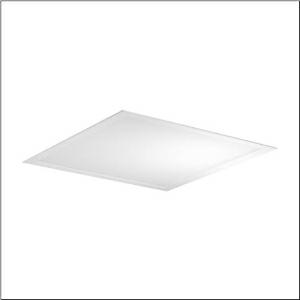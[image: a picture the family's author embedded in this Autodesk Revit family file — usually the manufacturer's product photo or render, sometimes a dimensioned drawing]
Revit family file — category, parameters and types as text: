
# Revit family: apollon_21_square_51mq11wd2114
name_source: partatom
category: Lighting Fixtures
units: mm (PartAtom-declared; Revit-internal decimal feet)

## family parameters
Cut with Voids When Loaded = No
Host = Face
Light Source = No
Part Type = Normal
Room Calculation Point = No
Round Connector Dimension = Use Diameter
Shared = No

## types (1)
- Apollon 21 square (1 x LED, 4100 lm, 24.7 W, 4000K)
    Apparent Load = 25 VA
    CIE Flux Codes = 60 87 97 100 100
    Color Rendering = 90
    Color Temperature = 4000K
    Default Elevation = 1800 mm
    Description = Apollon 21 square, office luminaire, primary optical cover: micro prismatic cover, of PMMA, CAT 2 (L<= 3000cd/m²), light emission: direct distribution, primary light characteristic: symmetric, installation type: lay-in mounting, recessed, LED, rated luminous flux: 4.100lm, luminous efficacy: 166lm/W, light colour: 940, colour temperature: 4000K, control gear: DALI 2, Multilumen, with terminal, 5-pole, mains connection: 220..240V, AC/DC, 0/50..60Hz, rated input power: 24.7W, suitable for self-contained emergency lighting element 59MQE002602A with integrated self-test function according to EN 60598-2-22, housing, of aluminium, coated, traffic white (RAL 9016), module: M625, length: 620mm, width: 620mm, height: 55mm, housing upper side, of sheet steel, galvanised, protection rating (complete): IP20, protection rating (lamp compartment, on room side): IP50, insulation class (complete): insulation class II (safety insulation), certification: CE, ENEC, UKCA, impact resistance: IK03, permissible operating ambient temperature: -20..+45°C, standard: EN 60598-2-22, corresponds to IFS (International Featured Standards) requirements for safety and quality in the food industry, packaging unit: 1 piece
    Height = 0 mm  [stored 0 ft]
    Lamp = 1 x LED
    Lamp Light Flux = 4100 lm
    Lamp Power = 24.7 W
    Lamp count = 1
    Length = 620 mm
    Luminous efficacy = 166 lm/W
    Manufacturer = Siteco
    ModVariant = No
    Model = 51MQ11WD2114
    Mounting Place = Ceiling
    Mounting Type = Recessed
    Number of Poles = 1
    OnlyDefault = Yes
    Power Factor = 1
    Product Name = Apollon 21 square
    Product group = office luminaire | ceiling recessed
    ProductGroupID = 400
    Protection Class = Protection class II
    Protection Degree = IP 20
    RLX_Detail_Level = 1
    RLX_Emergency_Light_Flux = 0 lm
    RLX_Emergency_Type = 0
    RLX_Emergency_Type_DB = No
    RlxData = <blob elided: 13293 chars, md5=ecd45b42>
    Socket = socket
    Standby Power = 0 W
    System Light Flux = 4100 lm
    System Power = 25 W
    Type Comments = Product without accessories
    Type Image = l_1291054.jpg
    URL = http://relux.com
    VarID = ---
    Voltage = 0 V
    Weight = 0.00 kg
    Width = 620 mm

note: [stored X ft] marks values corroborated as IEEE doubles in the binary element streams (Revit-internal decimal feet)

## geometry (parser evidence)
native form markers: Sweep x10
no freeform markers — native parametric forms only
